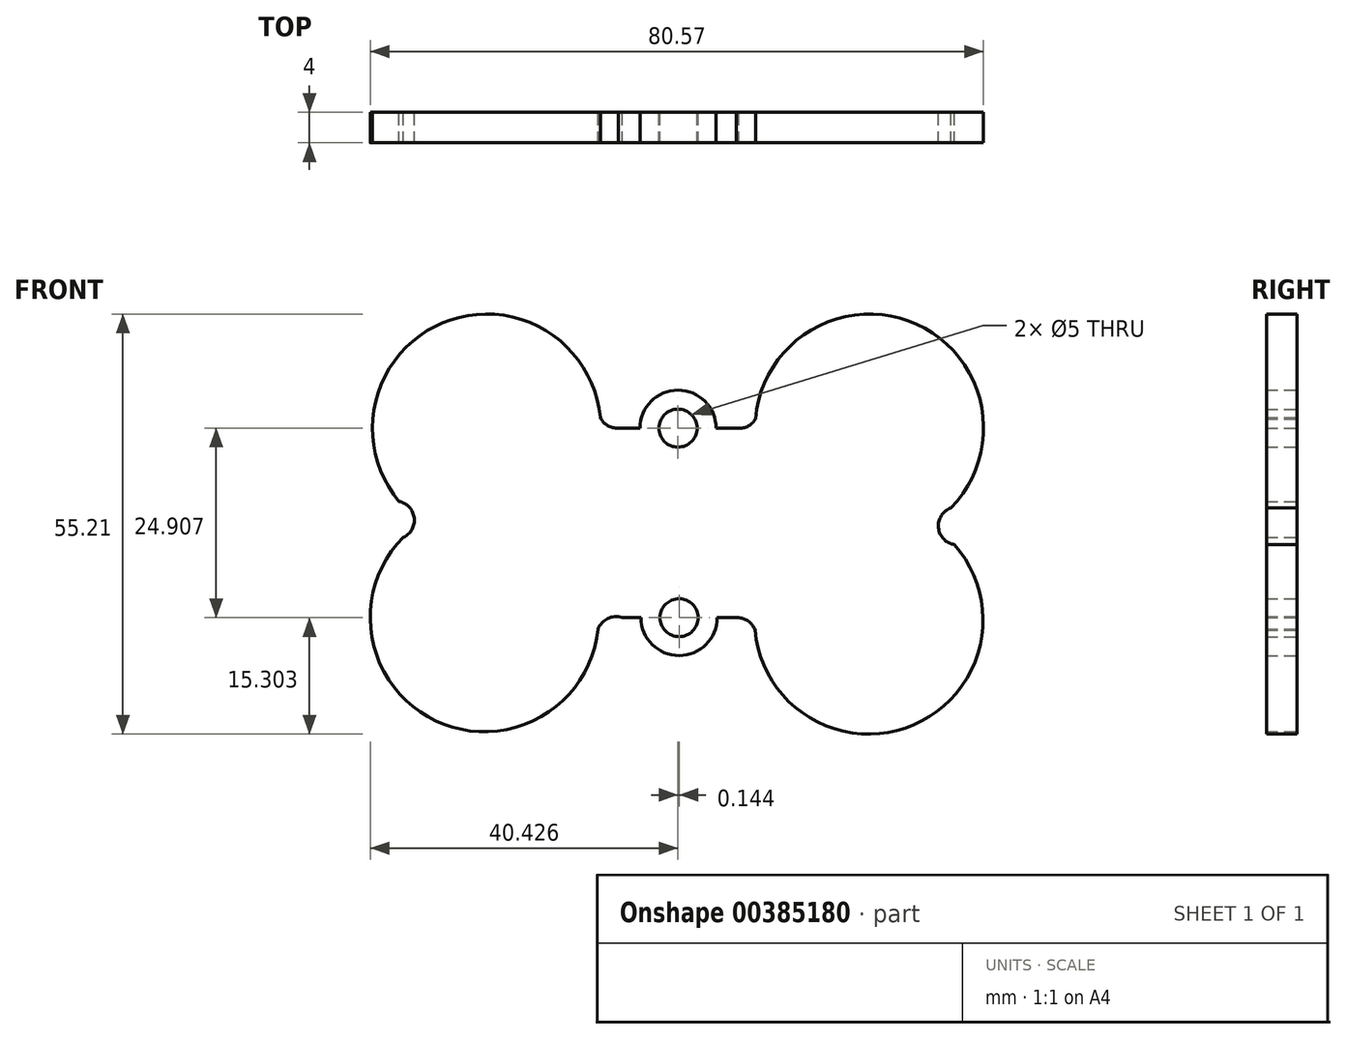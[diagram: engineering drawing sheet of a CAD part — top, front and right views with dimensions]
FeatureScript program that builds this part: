
annotation { "Feature Type Name" : "Feature", "Feature Type Description" : "" }
export const myFeature = defineFeature(function(context is Context, id is Id, definition is map)
    precondition{}
    {
        {
            var Q0;
            Q0=qCreatedBy(makeId("Front.planeOp"),FACE);
            var sketch = newSketch(context, id + "F0", { "sketchPlane" : qUnion([Q0])});
            skLineSegment(sketch, "E0.bottom", {"start": v(-8.24, 12.5) * mm, "end": v(-5.14, 12.5) * mm});
            skLineSegment(sketch, "E0.top", {"start": v(-7.5, -12.4) * mm, "end": v(-5, -12.4) * mm});
            skArc(sketch, "E1", {"start": v(-10.35, 13.88) * mm, "mid": v(-31.06, 26.35) * mm, "end": v(-36.78, 2.86) * mm});
            skArc(sketch, "E2", {"start": v(-36.23, -1.86) * mm, "mid": v(-31.97, -25.97) * mm, "end": v(-10.65, -13.92) * mm});
            skArc(sketch, "E3", {"start": v(9.97, -14.04) * mm, "mid": v(30.82, -26.5) * mm, "end": v(36.18, -2.81) * mm});
            skArc(sketch, "E4", {"start": v(4.86, 12.5) * mm, "mid": v(-0.14, 17.5) * mm, "end": v(-5.14, 12.5) * mm});
            skArc(sketch, "E5", {"start": v(-5, -12.4) * mm, "mid": v(0, -17.4) * mm, "end": v(5, -12.4) * mm});
            skCircle(sketch, "E6", {"center": v(-0.14, 12.5) * mm, "radius": 2.5 * mm});
            skCircle(sketch, "E7", {"center": v(0, -12.4) * mm, "radius": 2.5 * mm});
            skLineSegment(sketch, "E8.trimOffspring", {"start": v(4.86, 12.5) * mm, "end": v(8.26, 12.5) * mm});
            skArc(sketch, "E9", {"start": v(-10.35, 13.88) * mm, "mid": v(-9.27, 12.78) * mm, "end": v(-7.76, 12.52) * mm});
            skArc(sketch, "E10", {"start": v(7.5, 12.5) * mm, "mid": v(8.96, 12.72) * mm, "end": v(10.05, 13.73) * mm});
            skLineSegment(sketch, "E11.trimOffspring", {"start": v(5, -12.4) * mm, "end": v(7.83, -12.4) * mm});
            skArc(sketch, "E12", {"start": v(9.97, -14.04) * mm, "mid": v(8.98, -12.8) * mm, "end": v(7.43, -12.4) * mm});
            skArc(sketch, "E13", {"start": v(-7.5, -12.4) * mm, "mid": v(-9.38, -12.52) * mm, "end": v(-10.65, -13.92) * mm});
            skArc(sketch, "E14", {"start": v(-36.23, -1.86) * mm, "mid": v(-34.8, 0.7) * mm, "end": v(-36.78, 2.86) * mm});
            skArc(sketch, "E15", {"start": v(35.73, 2.02) * mm, "mid": v(34.07, -0.58) * mm, "end": v(36.18, -2.81) * mm});
            skArc(sketch, "E16.trimOffspring", {"start": v(35.73, 2.02) * mm, "mid": v(31.22, 26.15) * mm, "end": v(10.05, 13.73) * mm});
            skSolve(sketch);
        }
        {
            var Q0;
            Q0=makeQuery(id+"F0.imprint","IMPRINT",FACE,{"disambiguationData":[TD([[makeQuery(id+"F0.imprint","IMPRINT",EDGE,{"derivedFrom":sQuery(id+"F0.wireOp",EDGE,"E0.top")}),1.0]])]});
            extrude(context, id + "F1", {"entities" : qUnion([Q0]), "depth" : 4 * mm});
        }
    });
